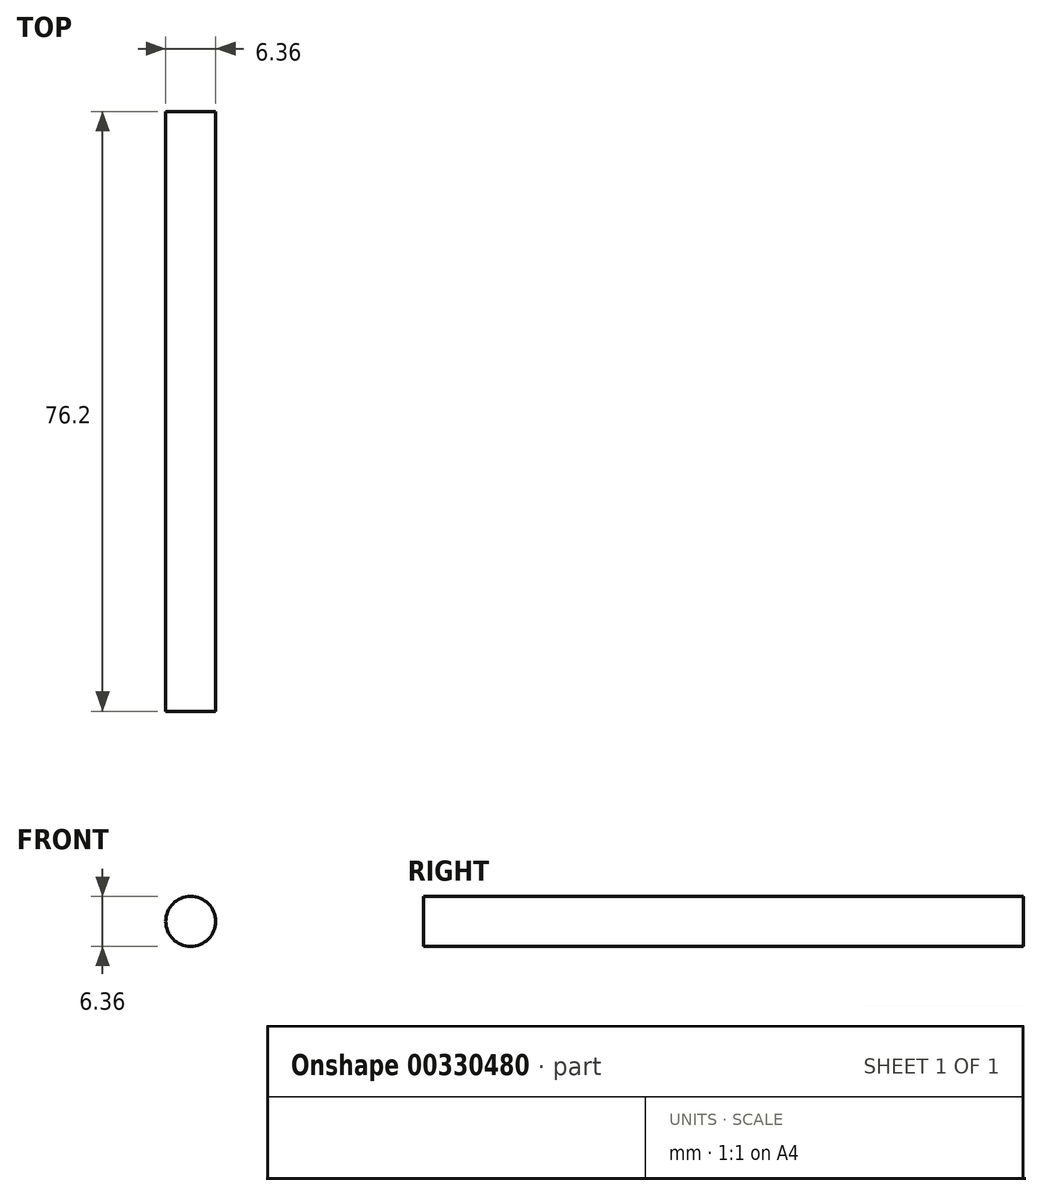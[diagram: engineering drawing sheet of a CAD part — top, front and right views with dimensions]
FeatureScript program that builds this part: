
annotation { "Feature Type Name" : "Feature", "Feature Type Description" : "" }
export const myFeature = defineFeature(function(context is Context, id is Id, definition is map)
    precondition{}
    {
        {
            var Q0;
            Q0=qCreatedBy(makeId("Front.planeOp"),FACE);
            var sketch = newSketch(context, id + "F0", { "sketchPlane" : qUnion([Q0])});
            skCircle(sketch, "E0", {"center": v(0, 0) * mm, "radius": 3.18 * mm});
            skSolve(sketch);
        }
        {
            var Q0;
            Q0=qSketchRegion(id+"F0",true);
            extrude(context, id + "F1", {"entities" : qUnion([Q0]), "depth" : 76.2 * mm});
        }
        {
            var Q0;
            Q0=makeQuery(id+"F1.opExtrude","SWEPT_BODY",BODY,{"disambiguationData":[OSD([sQuery(id+"F0.wireOp",EDGE,"E0")])]});
            transform(context, id + "F2", {"entities" : qUnion([Q0]), "transformType" : TransformType.TRANSLATION_3D, "dx" : 0 * mm, "dy" : 0 * mm, "dz" : 0 * mm, "makeCopy" : true});
        }
    });
